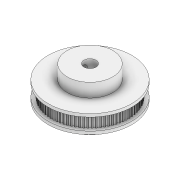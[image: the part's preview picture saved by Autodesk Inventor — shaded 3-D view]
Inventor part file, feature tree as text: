
AUTODESK INVENTOR PART (.ipt)
format: ipt  version: 2020 (Build 240168000, 168)  size: 611,328 bytes
history: native  units: mm
features: mirror x1
ambient origin geometry x8: Origin, YZ Plane, XZ Plane, XY Plane, X Axis, Y Axis, Z Axis, Center Point
bodies: Solid1 (feature_tree)
feature tree (1):
  mirror  "Mirror1"
